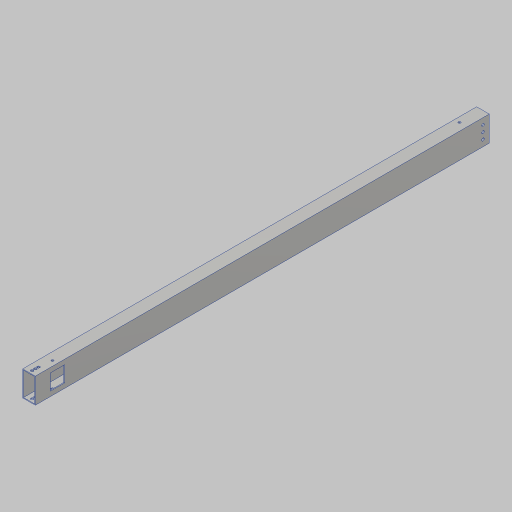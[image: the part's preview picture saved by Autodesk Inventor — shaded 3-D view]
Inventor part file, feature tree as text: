
AUTODESK INVENTOR PART (.ipt)
format: ipt  version: 2023.5 (Build 275446000, 446)  size: 314,880 bytes
history: native  units: in
note: dims shown in document units (in); Inventor stores cm internally (conversion verified against a paired STEP export)
features: sketch x6, hole x4, extrude x3
ambient origin geometry x8: Origin, YZ Plane, XZ Plane, XY Plane, X Axis, Y Axis, Z Axis, Center Point
bodies: Solid1 (feature_tree)
feature tree (13):
  extrude  "Extrusion1"  Depth=0.25in
  hole  "Hole1"  [1 undecoded]
  hole  "Hole2"  [1 undecoded]
  hole  "Hole3"  [1 undecoded]
  hole  "Hole4"  [1 undecoded]
  extrude  "Extrusion2"  Depth=1.0in
  extrude  "Extrusion3"  Depth=1.0in
  sketch  "Sketch2"  dims[d4=0.0in d5=0.25in]
  sketch  "Sketch3"  dims[d6=0.25in d7=0.25in]
  sketch  "Sketch4"  dims[d8=0.201in d9=0.38in d10=0.385in d11=0.25in d12=0.5635in d13=1.0in d14=0.8108in d15=0.5in]
  sketch  "Sketch5"  dims[d16=0.5in d17=0.5in]
  sketch  "Sketch6"  dims[d18=0.201in d19=0.75in d20=0.385in d21=0.25in d22=0.5635in d23=1.0in d24=0.8108in]
  sketch  "Sketch7"  dims[d27=0.175in d28=0.75in d29=0.385in d30=0.25in d31=0.5635in d32=1.0in d33=0.8108in d34=0.391in d35=1.75in d36=0.391in d37=0.175in d38=0.75in d39=0.375in d40=0.25in d41=0.5635in d42=1.0in d43=0.8108in d44=1.2in d45=1.1in d47=1.25in d48=0.0625in d49=0.0in d50=1.2in d51=1.25in d52=1.1in d53=0.0625in d54=0.0in d55=1.0in d26=1.0in]
note: 4 required parameter values undecoded (feature->parameter linkage not recoverable at this tier; creation-order binding heuristic only, values carry confidence <= 0.55)
